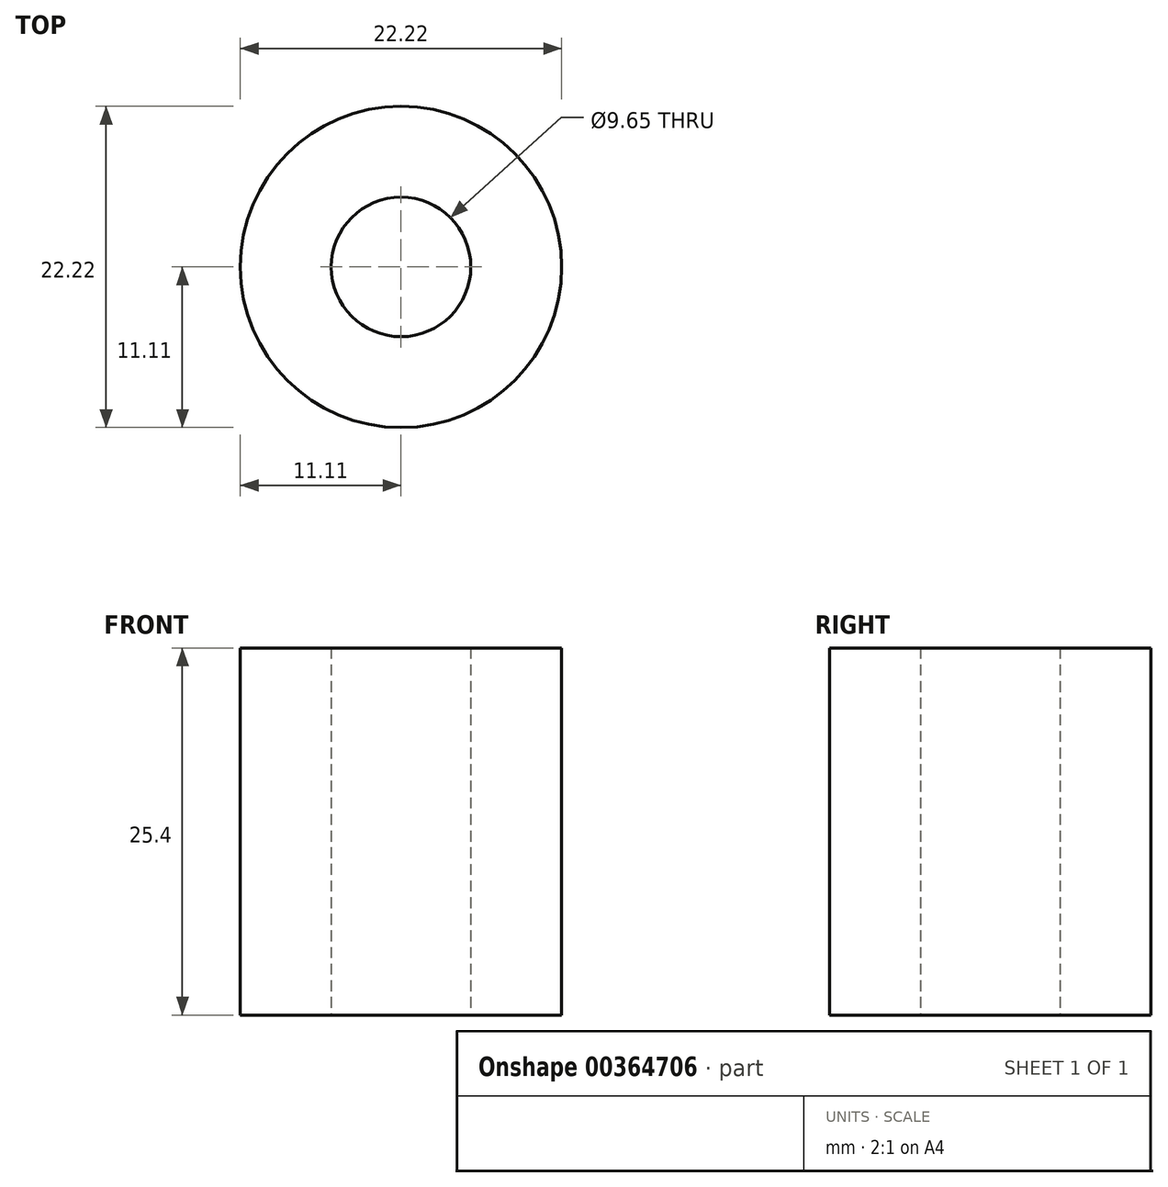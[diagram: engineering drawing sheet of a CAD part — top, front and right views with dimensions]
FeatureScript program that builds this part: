
annotation { "Feature Type Name" : "Feature", "Feature Type Description" : "" }
export const myFeature = defineFeature(function(context is Context, id is Id, definition is map)
    precondition{}
    {
        {
            var Q0;
            Q0=qCreatedBy(makeId("Top.planeOp"),FACE);
            var sketch = newSketch(context, id + "F0", { "sketchPlane" : qUnion([Q0])});
            skCircle(sketch, "E0", {"center": v(0, 0) * mm, "radius": 11.11 * mm});
            skCircle(sketch, "E1", {"center": v(0, 0) * mm, "radius": 4.83 * mm});
            skSolve(sketch);
        }
        {
            var Q0;
            Q0 = qSketchRegion(id + "F0", true);
            extrude(context, id + "F1", {"entities" : qUnion([Q0]), "depth" : 25.4 * mm, "offsetDistance" : 25.4 * mm});
        }
    });
